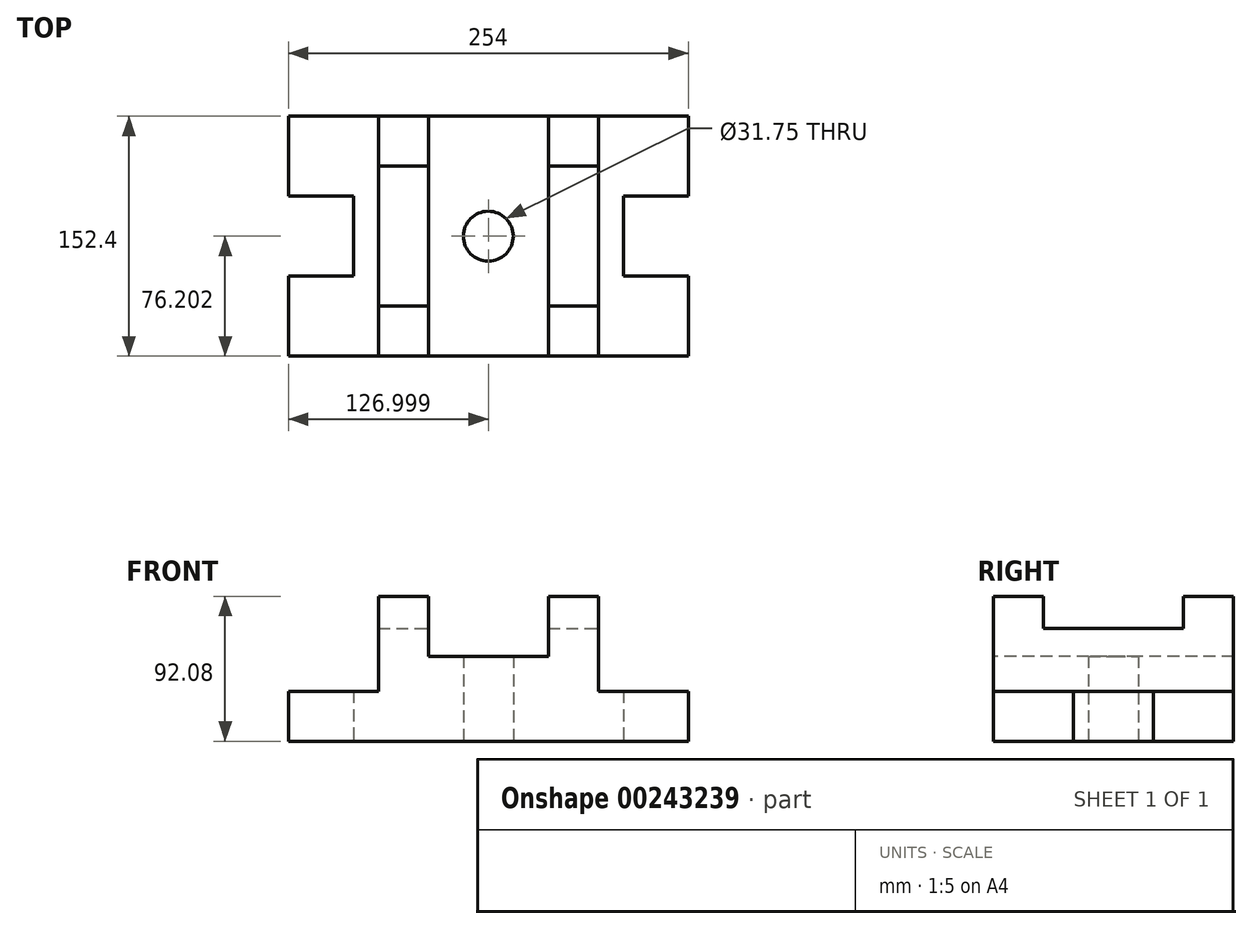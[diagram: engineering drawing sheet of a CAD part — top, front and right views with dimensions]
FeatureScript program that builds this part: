
annotation { "Feature Type Name" : "Feature", "Feature Type Description" : "" }
export const myFeature = defineFeature(function(context is Context, id is Id, definition is map)
    precondition{}
    {
        {
            var Q0;
            Q0=qCreatedBy(makeId("Top.planeOp"),FACE);
            var sketch = newSketch(context, id + "F0", { "sketchPlane" : qUnion([Q0])});
            skLineSegment(sketch, "E0", {"start": v(150.1, -48.12) * mm, "end": v(150.1, 2.68) * mm});
            skLineSegment(sketch, "E1", {"start": v(150.1, 2.68) * mm, "end": v(108.83, 2.68) * mm});
            skLineSegment(sketch, "E2", {"start": v(108.83, 2.68) * mm, "end": v(108.83, 53.48) * mm});
            skLineSegment(sketch, "E3", {"start": v(108.83, 53.48) * mm, "end": v(150.1, 53.48) * mm});
            skLineSegment(sketch, "E4", {"start": v(150.1, 53.48) * mm, "end": v(150.1, 104.28) * mm});
            skLineSegment(sketch, "E5", {"start": v(150.1, 104.28) * mm, "end": v(-103.9, 104.28) * mm});
            skLineSegment(sketch, "E6", {"start": v(-103.9, 104.28) * mm, "end": v(-103.9, 53.48) * mm});
            skLineSegment(sketch, "E7", {"start": v(-103.9, 53.48) * mm, "end": v(-62.62, 53.48) * mm});
            skLineSegment(sketch, "E8", {"start": v(-62.62, 53.48) * mm, "end": v(-62.62, 2.68) * mm});
            skLineSegment(sketch, "E9", {"start": v(-62.62, 2.68) * mm, "end": v(-103.9, 2.68) * mm});
            skLineSegment(sketch, "E10", {"start": v(-103.9, 2.68) * mm, "end": v(-103.9, -48.12) * mm});
            skLineSegment(sketch, "E11", {"start": v(-103.9, -48.12) * mm, "end": v(150.1, -48.12) * mm});
            skLineSegment(sketch, "E12", {"start": v(-46.74, 104.28) * mm, "end": v(-46.74, -48.12) * mm});
            skLineSegment(sketch, "E13", {"start": v(92.96, 104.28) * mm, "end": v(92.96, -48.12) * mm});
            skLineSegment(sketch, "E14", {"start": v(-15, 104.28) * mm, "end": v(-15, -48.12) * mm});
            skLineSegment(sketch, "E15", {"start": v(61.2, 104.28) * mm, "end": v(61.2, -48.12) * mm});
            skLineSegment(sketch, "E16", {"start": v(-46.74, 72.53) * mm, "end": v(-15, 72.53) * mm});
            skLineSegment(sketch, "E17", {"start": v(-46.74, -16.37) * mm, "end": v(-15, -16.37) * mm});
            skLineSegment(sketch, "E18", {"start": v(61.2, 72.53) * mm, "end": v(92.96, 72.53) * mm});
            skLineSegment(sketch, "E19", {"start": v(61.2, -16.37) * mm, "end": v(92.96, -16.37) * mm});
            skCircle(sketch, "E20", {"center": v(23.1, 28.08) * mm, "radius": 15.88 * mm});
            skSolve(sketch);
        }
        {
            var Q0;
            {var subQ4=sQuery(id+"F0.wireOp",EDGE,"E0");Q0=makeQuery(id+"F0.imprint","IMPRINT",FACE,{"disambiguationData":[TD([[makeQuery(id+"F0.imprint","IMPRINT",EDGE,{"derivedFrom":subQ4}),1.0]])]});}
            var Q1;
            {var subQ0=sQuery(id+"F0.wireOp",EDGE,"E6");Q1=makeQuery(id+"F0.imprint","IMPRINT",FACE,{"disambiguationData":[TD([[makeQuery(id+"F0.imprint","IMPRINT",EDGE,{"derivedFrom":subQ0}),1.0]])]});}
            extrude(context, id + "F1", {"entities" : qUnion([Q0, Q1]), "depth" : 31.75 * mm});
        }
        {
            var Q0;
            Q0=makeQuery(id+"F0.imprint","IMPRINT",FACE,{"disambiguationData":[TD([[makeQuery(id+"F0.imprint","IMPRINT",EDGE,{"derivedFrom":sQuery(id+"F0.wireOp",EDGE,"E20")}),-1.0]])]});
            extrude(context, id + "F2", {"entities" : qUnion([Q0]), "operationType" : NewBodyOperationType.ADD, "depth" : 53.97 * mm});
        }
        {
            var Q0;
            {var subQ0=sQuery(id+"F0.wireOp",EDGE,"E16");Q0=makeQuery(id+"F0.imprint","IMPRINT",FACE,{"disambiguationData":[TD([[makeQuery(id+"F0.imprint","IMPRINT",EDGE,{"derivedFrom":subQ0}),-1.0]])]});}
            var Q1;
            {var subQ0=sQuery(id+"F0.wireOp",EDGE,"E18");Q1=makeQuery(id+"F0.imprint","IMPRINT",FACE,{"disambiguationData":[TD([[makeQuery(id+"F0.imprint","IMPRINT",EDGE,{"derivedFrom":subQ0}),-1.0]])]});}
            extrude(context, id + "F3", {"entities" : qUnion([Q0, Q1]), "operationType" : NewBodyOperationType.ADD, "depth" : 71.75 * mm});
        }
        {
            var Q0;
            {var subQ5=sQuery(id+"F0.wireOp",EDGE,"E16");Q0=makeQuery(id+"F0.imprint","IMPRINT",FACE,{"disambiguationData":[TD([[makeQuery(id+"F0.imprint","IMPRINT",EDGE,{"derivedFrom":subQ5}),1.0]])]});}
            var Q1;
            {var subQ5=sQuery(id+"F0.wireOp",EDGE,"E17");Q1=makeQuery(id+"F0.imprint","IMPRINT",FACE,{"disambiguationData":[TD([[makeQuery(id+"F0.imprint","IMPRINT",EDGE,{"derivedFrom":subQ5}),-1.0]])]});}
            var Q2;
            {var subQ5=sQuery(id+"F0.wireOp",EDGE,"E19");Q2=makeQuery(id+"F0.imprint","IMPRINT",FACE,{"disambiguationData":[TD([[makeQuery(id+"F0.imprint","IMPRINT",EDGE,{"derivedFrom":subQ5}),-1.0]])]});}
            var Q3;
            {var subQ5=sQuery(id+"F0.wireOp",EDGE,"E18");Q3=makeQuery(id+"F0.imprint","IMPRINT",FACE,{"disambiguationData":[TD([[makeQuery(id+"F0.imprint","IMPRINT",EDGE,{"derivedFrom":subQ5}),1.0]])]});}
            extrude(context, id + "F4", {"entities" : qUnion([Q0, Q1, Q2, Q3]), "operationType" : NewBodyOperationType.ADD, "depth" : 92.07 * mm});
        }
    });
